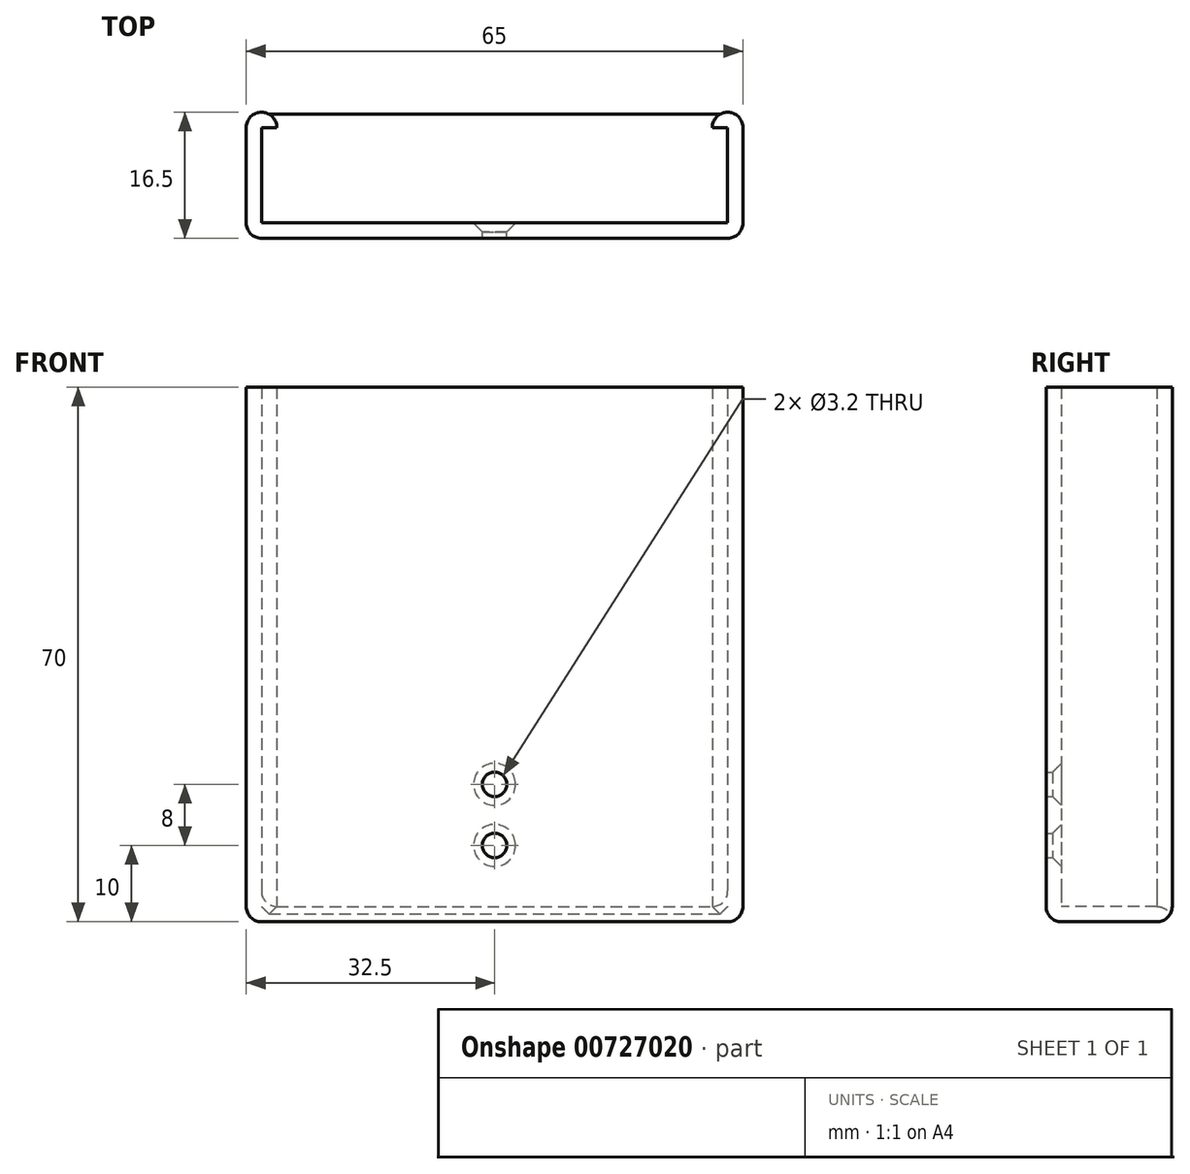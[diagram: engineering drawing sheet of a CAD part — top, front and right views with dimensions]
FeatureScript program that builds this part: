
annotation { "Feature Type Name" : "Feature", "Feature Type Description" : "" }
export const myFeature = defineFeature(function(context is Context, id is Id, definition is map)
    precondition{}
    {
        {
            var Q0;
            Q0=qCreatedBy(makeId("Top.planeOp"),FACE);
            var sketch = newSketch(context, id + "F7", { "sketchPlane" : qUnion([Q0])});
            skLineSegment(sketch, "E0", {"start": v(-32.5, 0) * mm, "end": v(32.5, 0) * mm});
            skLineSegment(sketch, "E1", {"start": v(32.5, 0) * mm, "end": v(32.5, 16.5) * mm});
            skLineSegment(sketch, "E2", {"start": v(32.5, 16.5) * mm, "end": v(28.5, 16.5) * mm});
            skLineSegment(sketch, "E3", {"start": v(28.5, 16.5) * mm, "end": v(28.5, 14.5) * mm});
            skLineSegment(sketch, "E4", {"start": v(28.5, 14.5) * mm, "end": v(30.5, 14.5) * mm});
            skLineSegment(sketch, "E5", {"start": v(30.5, 14.5) * mm, "end": v(30.5, 2) * mm});
            skLineSegment(sketch, "E6", {"start": v(30.5, 2) * mm, "end": v(-30.5, 2) * mm});
            skLineSegment(sketch, "E7", {"start": v(-30.5, 2) * mm, "end": v(-30.5, 14.5) * mm});
            skLineSegment(sketch, "E8", {"start": v(-30.5, 14.5) * mm, "end": v(-28.5, 14.5) * mm});
            skLineSegment(sketch, "E9", {"start": v(-28.5, 14.5) * mm, "end": v(-28.5, 16.5) * mm});
            skLineSegment(sketch, "E10", {"start": v(-28.5, 16.5) * mm, "end": v(-32.5, 16.5) * mm});
            skLineSegment(sketch, "E11", {"start": v(-32.5, 16.5) * mm, "end": v(-32.5, 0) * mm});
            skSolve(sketch);
        }
        {
            var Q0;
            Q0=qSketchRegion(id+"FxWtbJgkQHIbVw/JA_0",true);
            var Q1;
            Q1=makeQuery(id+"F7.imprint","IMPRINT",FACE,{"disambiguationData":[TD([[makeQuery(id+"F7.imprint","IMPRINT",EDGE,{"derivedFrom":sQuery(id+"F7.wireOp",EDGE,"E0")}),1.0]])]});
            extrude(context, id + "F0", {"entities" : qUnion([Q0, Q1]), "depth" : 70 * mm});
        }
        {
            var Q0;
            Q0=makeQuery(id+"F0.opExtrude","CAP_FACE",FACE,{"disambiguationData":[OSD([sQuery(id+"F7.wireOp",EDGE,"E0"),sQuery(id+"F7.wireOp",EDGE,"E1"),sQuery(id+"F7.wireOp",EDGE,"E2"),sQuery(id+"F7.wireOp",EDGE,"E3"),sQuery(id+"F7.wireOp",EDGE,"E4"),sQuery(id+"F7.wireOp",EDGE,"E5"),sQuery(id+"F7.wireOp",EDGE,"E6"),sQuery(id+"F7.wireOp",EDGE,"E7"),sQuery(id+"F7.wireOp",EDGE,"E8"),sQuery(id+"F7.wireOp",EDGE,"E9"),sQuery(id+"F7.wireOp",EDGE,"E10"),sQuery(id+"F7.wireOp",EDGE,"E11")])],"isStart":true});
            var sketch = newSketch(context, id + "F1", { "sketchPlane" : qUnion([Q0])});
            skLineSegment(sketch, "E12.bottom", {"start": v(32.5, -16.5) * mm, "end": v(-32.5, -16.5) * mm});
            skLineSegment(sketch, "E12.top", {"start": v(32.5, 0) * mm, "end": v(-32.5, 0) * mm});
            skLineSegment(sketch, "E12.left", {"start": v(32.5, -16.5) * mm, "end": v(32.5, 0) * mm});
            skLineSegment(sketch, "E12.right", {"start": v(-32.5, -16.5) * mm, "end": v(-32.5, 0) * mm});
            skSolve(sketch);
        }
        {
            var Q0;
            Q0=qSketchRegion(id+"F1",true);
            extrude(context, id + "F8", {"entities" : qUnion([Q0]), "operationType" : NewBodyOperationType.ADD, "oppositeDirection" : true, "depth" : 2 * mm});
        }
        {
            var Q0;
            Q0=makeQuery(id+"F0.opExtrude","CAP_EDGE",EDGE,{"disambiguationData":[OSD([sQuery(id+"F7.wireOp",EDGE,"E1")])],"isStart":true});
            var Q1;
            Q1=makeQuery(id+"F0.opExtrude","CAP_EDGE",EDGE,{"disambiguationData":[OSD([sQuery(id+"F7.wireOp",EDGE,"E11")])],"isStart":true});
            var Q2;
            Q2=makeQuery(id+"F8.boolean.opBoolean","INTERSECT",EDGE,{"derivedFrom":[makeQuery(id+"F0.opExtrude","SWEPT_FACE",FACE,{"disambiguationData":[OSD([sQuery(id+"F7.wireOp",EDGE,"E5")])]}),makeQuery(id+"F8.opExtrude","CAP_FACE",FACE,{"disambiguationData":[OSD([sQuery(id+"F1.wireOp",EDGE,"E12.bottom"),sQuery(id+"F1.wireOp",EDGE,"E12.top"),sQuery(id+"F1.wireOp",EDGE,"E12.left"),sQuery(id+"F1.wireOp",EDGE,"E12.right")])],"isStart":false})]});
            var Q3;
            Q3=makeQuery(id+"F8.boolean.opBoolean","INTERSECT",EDGE,{"derivedFrom":[makeQuery(id+"F0.opExtrude","SWEPT_FACE",FACE,{"disambiguationData":[OSD([sQuery(id+"F7.wireOp",EDGE,"E7")])]}),makeQuery(id+"F8.opExtrude","CAP_FACE",FACE,{"disambiguationData":[OSD([sQuery(id+"F1.wireOp",EDGE,"E12.bottom"),sQuery(id+"F1.wireOp",EDGE,"E12.top"),sQuery(id+"F1.wireOp",EDGE,"E12.left"),sQuery(id+"F1.wireOp",EDGE,"E12.right")])],"isStart":false})]});
            var Q4;
            Q4=makeQuery(id+"F0.opExtrude","SWEPT_EDGE",EDGE,{"disambiguationData":[OSD([sQuery(id+"F7.wireOp",EDGE,"E0"),sQuery(id+"F7.wireOp",EDGE,"E11")])]});
            var Q5;
            Q5=makeQuery(id+"F0.opExtrude","SWEPT_EDGE",EDGE,{"disambiguationData":[OSD([sQuery(id+"F7.wireOp",EDGE,"E0"),sQuery(id+"F7.wireOp",EDGE,"E1")])]});
            var Q6;
            Q6=makeQuery(id+"F0.opExtrude","SWEPT_EDGE",EDGE,{"disambiguationData":[OSD([sQuery(id+"F7.wireOp",EDGE,"E10"),sQuery(id+"F7.wireOp",EDGE,"E11")])]});
            var Q7;
            Q7=makeQuery(id+"F0.opExtrude","SWEPT_EDGE",EDGE,{"disambiguationData":[OSD([sQuery(id+"F7.wireOp",EDGE,"E1"),sQuery(id+"F7.wireOp",EDGE,"E2")])]});
            var Q8;
            Q8=makeQuery(id+"F0.opExtrude","SWEPT_EDGE",EDGE,{"disambiguationData":[OSD([sQuery(id+"F7.wireOp",EDGE,"E9"),sQuery(id+"F7.wireOp",EDGE,"E10")])]});
            var Q9;
            Q9=makeQuery(id+"F8.opExtrude","CAP_EDGE",EDGE,{"disambiguationData":[OSD([sQuery(id+"F1.wireOp",EDGE,"E12.bottom")])],"isStart":false});
            var Q10;
            Q10=makeQuery(id+"F0.opExtrude","SWEPT_EDGE",EDGE,{"disambiguationData":[OSD([sQuery(id+"F7.wireOp",EDGE,"E2"),sQuery(id+"F7.wireOp",EDGE,"E3")])]});
            var Q11;
            Q11=makeQuery(id+"F0.opExtrude","CAP_EDGE",EDGE,{"disambiguationData":[OSD([sQuery(id+"F7.wireOp",EDGE,"E0")])],"isStart":true});
            var Q12;
            Q12=makeQuery(id+"F8.boolean.opBoolean","MERGE",EDGE,{"derivedFrom":[makeQuery(id+"F0.opExtrude","CAP_EDGE",EDGE,{"disambiguationData":[OSD([sQuery(id+"F7.wireOp",EDGE,"E2")])],"isStart":true}),makeQuery(id+"F0.opExtrude","CAP_EDGE",EDGE,{"disambiguationData":[OSD([sQuery(id+"F7.wireOp",EDGE,"E10")])],"isStart":true}),makeQuery(id+"F8.opExtrude","CAP_EDGE",EDGE,{"disambiguationData":[OSD([sQuery(id+"F1.wireOp",EDGE,"E12.bottom")])],"isStart":true})]});
            fillet(context, id + "F2", {"entities" : qUnion([Q0, Q1, Q2, Q3, Q4, Q5, Q6, Q7, Q8, Q9, Q10, Q11, Q12]), "radius" : 2 * mm, "tangentPropagation" : true, "allowEdgeOverflow" : false});
        }
        {
            var Q0;
            Q0=qCreatedBy(makeId("Front.planeOp"),FACE);
            var sketch = newSketch(context, id + "F3", { "sketchPlane" : qUnion([Q0])});
            skSolve(sketch);
        }
        {
            var Q0;
            Q0=makeQuery(id+"F0.opExtrude","SWEPT_FACE",FACE,{"disambiguationData":[OSD([sQuery(id+"F7.wireOp",EDGE,"E6")])]});
            var sketch = newSketch(context, id + "F4", { "sketchPlane" : qUnion([Q0])});
            skPoint(sketch, "E13.positionSnap0", {"position": v(0, 2) * mm});
            skPoint(sketch, "E14", {"position": v(0, 18) * mm});
            skPoint(sketch, "E15", {"position": v(0, 10) * mm});
            skSolve(sketch);
        }
        {
            var Q0;
            Q0=sQuery(id+"F4.wireOp",VERTEX,"E14");
            var Q1;
            Q1=makeQuery(id+"F0.opExtrude","SWEPT_BODY",BODY,{"disambiguationData":[OSD([sQuery(id+"F7.wireOp",EDGE,"E0"),sQuery(id+"F7.wireOp",EDGE,"E1"),sQuery(id+"F7.wireOp",EDGE,"E2"),sQuery(id+"F7.wireOp",EDGE,"E3"),sQuery(id+"F7.wireOp",EDGE,"E4"),sQuery(id+"F7.wireOp",EDGE,"E5"),sQuery(id+"F7.wireOp",EDGE,"E6"),sQuery(id+"F7.wireOp",EDGE,"E7"),sQuery(id+"F7.wireOp",EDGE,"E8"),sQuery(id+"F7.wireOp",EDGE,"E9"),sQuery(id+"F7.wireOp",EDGE,"E10"),sQuery(id+"F7.wireOp",EDGE,"E11")])]});
            hole(context, id + "F5", {"style" : HoleStyle.C_SINK, "endStyle" : HoleEndStyle.THROUGH, "holeDiameter" : 3.2 * mm, "cSinkDiameter" : 5.5 * mm, "cSinkAngle" : 90 * degree, "majorDiameter" : 5 * mm, "isTappedThrough" : true, "tappedDepth" : 12 * mm, "tapClearance" : 3, "locations" : qUnion([Q0]), "scope" : qUnion([Q1])});
        }
        {
            var Q0;
            Q0=sQuery(id+"F4.wireOp",VERTEX,"E15");
            var Q1;
            Q1=makeQuery(id+"F0.opExtrude","SWEPT_BODY",BODY,{"disambiguationData":[OSD([sQuery(id+"F7.wireOp",EDGE,"E0"),sQuery(id+"F7.wireOp",EDGE,"E1"),sQuery(id+"F7.wireOp",EDGE,"E2"),sQuery(id+"F7.wireOp",EDGE,"E3"),sQuery(id+"F7.wireOp",EDGE,"E4"),sQuery(id+"F7.wireOp",EDGE,"E5"),sQuery(id+"F7.wireOp",EDGE,"E6"),sQuery(id+"F7.wireOp",EDGE,"E7"),sQuery(id+"F7.wireOp",EDGE,"E8"),sQuery(id+"F7.wireOp",EDGE,"E9"),sQuery(id+"F7.wireOp",EDGE,"E10"),sQuery(id+"F7.wireOp",EDGE,"E11")])]});
            hole(context, id + "F6", {"style" : HoleStyle.C_SINK, "endStyle" : HoleEndStyle.THROUGH, "holeDiameter" : 3.2 * mm, "cSinkDiameter" : 5.5 * mm, "cSinkAngle" : 90 * degree, "majorDiameter" : 5 * mm, "isTappedThrough" : true, "tappedDepth" : 12 * mm, "tapClearance" : 3, "locations" : qUnion([Q0]), "scope" : qUnion([Q1])});
        }
    });
